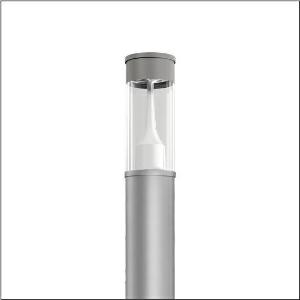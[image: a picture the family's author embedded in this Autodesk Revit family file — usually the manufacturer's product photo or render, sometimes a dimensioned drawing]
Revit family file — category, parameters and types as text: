
# Revit family: city-light_260_iq___pl1_2s_5xa5295cf14h_efd3
name_source: partatom
category: Lighting Fixtures
units: mm (PartAtom-declared; Revit-internal decimal feet)

## family parameters
Cut with Voids When Loaded = No
Host = Face
Light Source = No
Part Type = Normal
Room Calculation Point = No
Round Connector Dimension = Use Diameter
Shared = No

## types (1)
- --- (1 x LED, 2970 lm, 23.9 W, 2200K)
    Apparent Load = 24 VA
    CIE Flux Codes = 23 62 94 96 100
    Color Rendering = 70
    Color Temperature = 2200K
    Default Elevation = 1800 mm
    Description = City-Light 260 iQ, light pillar, Module 540 iQ-SR, primary light control with 3 zone facetted reflector, of plastic, silver coated, highly specular, structured, primary optical cover: cover, of PMMA, transparent, partly coated, light distribution: PL1.2s, primary light characteristic: symmetric, LED, High Power LED, rated luminous flux: 2.970lm, luminous efficacy: 124lm/W, light colour: 722, colour temperature: 2200K, control gear: ECG iQ, control: presetting dimming logarithmic, Street-Remote, Auto-Match, Temp-Guard, Lumen-Switch, Night-Set, Smart-Wire, Light-Fading, Desk-Remote (wireless, voltage-free reading and setting of iQ features in the workshop via application-optimized NFC function/RFID function), optimised constant luminous flux control (CLO 2.0), with terminal, 6-pole, max. 2.5mm², mains connection: 230..240V, AC, 50/60Hz, start of lifetime: 24W, end of service life: 26W, reduction: 12W, luminaire housing, cylindrical, of extruded aluminium section, coated, Siteco® metallic grey (DB 702S), length: 2.600mm, diameter: 200mm, Module 540 iQ-SR, traffic white (RAL 9016), equipment: standard, protection rating (complete): IP65, insulation class (complete): insulation class II (safety insulation), certification: CE, ENEC, VDE, packaging unit: 1 piece

Light Distribution: PL1.2s
    Height = 500 mm
    Lamp = 1 x LED
    Lamp Light Flux = 2970 lm
    Lamp Power = 23.9 W
    Lamp count = 1
    Length = 200 mm  [stored 0.656168 ft]
    Luminous efficacy = 124 lm/W
    Manufacturer = Siteco
    ModVariant = No
    Model = 5XA5295CF14H
    Mounting Place = Floor
    Mounting Type = Freestanding
    Number of Poles = 1
    OnlyDefault = Yes
    Power Factor = 1
    Product Name = City-Light 260 iQ | PL1.2s
    Product group = light pillar
    ProductGroupID = 1303
    Protection Class = Protection class II
    Protection Degree = IP 65
    RLX_Detail_Level = 1
    RLX_Emergency_Light_Flux = 0 lm
    RLX_Emergency_Type = 0
    RLX_Emergency_Type_DB = No
    RlxData = <blob elided: 28853 chars, md5=34283a9c>
    Socket = socket
    Standby Power = 0 W
    System Light Flux = 2970 lm
    System Power = 24 W
    Type Comments = factory setting: luminous flux: 100 % | dim-lin: 254 | 499 mA
    Type Image = l_1006920.jpg
    URL = http://relux.com
    VarID = @adj_076703
    Voltage = 0 V
    Weight = 0.00 kg
    Width = 0 mm  [stored 0 ft]

note: [stored X ft] marks values corroborated as IEEE doubles in the binary element streams (Revit-internal decimal feet)

## geometry (parser evidence)
native form markers: Blend x4, Sweep x10
no freeform markers — native parametric forms only
